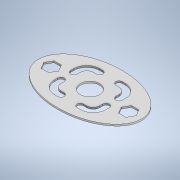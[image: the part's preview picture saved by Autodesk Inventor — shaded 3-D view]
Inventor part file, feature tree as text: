
AUTODESK INVENTOR PART (.ipt)
format: ipt  version: 2022.2 (Build 262287030, 287C)  size: 186,880 bytes
history: native  units: in
note: dims shown in document units (in); Inventor stores cm internally (conversion verified against a paired STEP export)
features: extrude x1, sketch x1
ambient origin geometry x8: Origin, YZ Plane, XZ Plane, XY Plane, X Axis, Y Axis, Z Axis, Center Point
bodies: Solid1 (feature_tree)
feature tree (2):
  extrude  "Extrusion1"  Depth=2.5in
  sketch  "Sketch1"  dims[d0=4.0in d1=2.5in d5=1.0in d6=0.75in d7=0.75in d8=0.25in d9=0.25in d10=1.5in d11=3.0in d12=1.0in d13=0.125in d14=0.0in]
